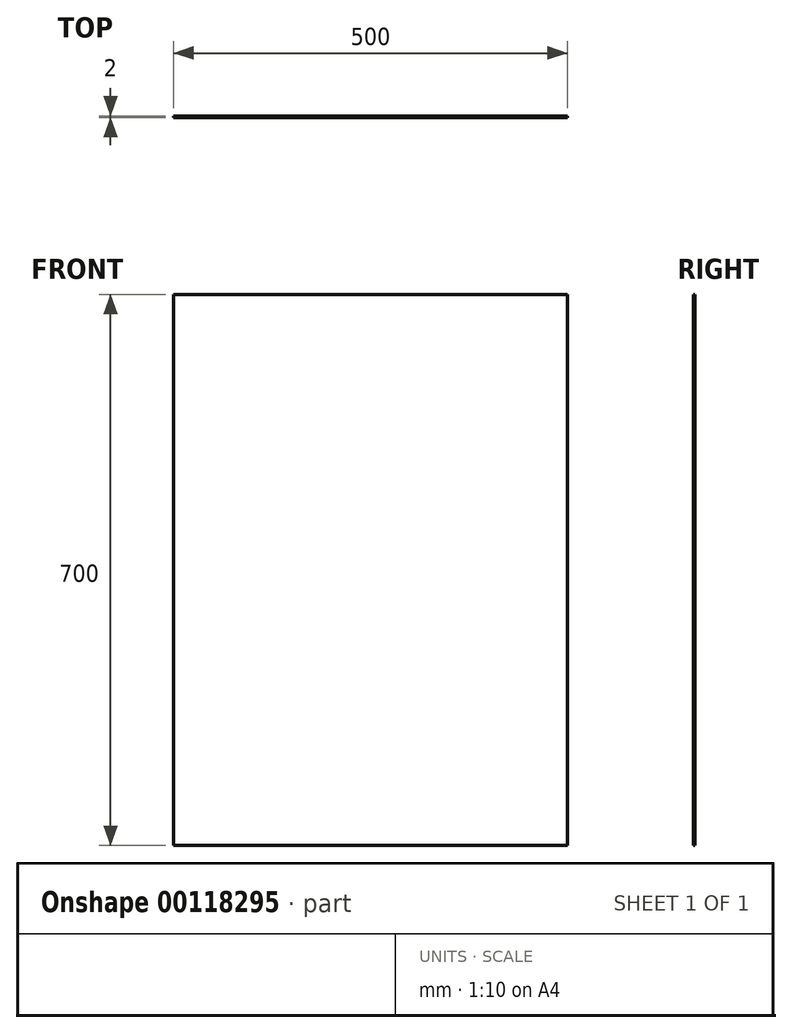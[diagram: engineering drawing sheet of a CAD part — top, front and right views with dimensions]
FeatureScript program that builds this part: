
annotation { "Feature Type Name" : "Feature", "Feature Type Description" : "" }
export const myFeature = defineFeature(function(context is Context, id is Id, definition is map)
    precondition{}
    {
        {
            var Q0;
            Q0=qCreatedBy(makeId("Front.planeOp"),FACE);
            var sketch = newSketch(context, id + "F0", { "sketchPlane" : qUnion([Q0])});
            skLineSegment(sketch, "E0.bottom", {"start": v(250, 350) * mm, "end": v(-250, 350) * mm});
            skLineSegment(sketch, "E0.top", {"start": v(250, -350) * mm, "end": v(-250, -350) * mm});
            skLineSegment(sketch, "E0.left", {"start": v(250, 350) * mm, "end": v(250, -350) * mm});
            skLineSegment(sketch, "E0.right", {"start": v(-250, 350) * mm, "end": v(-250, -350) * mm});
            skPoint(sketch, "E0.middle", {"position": v(0, 0) * mm});
            skSolve(sketch);
        }
        {
            var Q0;
            Q0 = qSketchRegion(id + "F0", true);
            var Q1;
            Q1=makeQuery(id+"F0.imprint","IMPRINT",FACE,{"disambiguationData":[TD([[makeQuery(id+"F0.imprint","IMPRINT",EDGE,{"derivedFrom":sQuery(id+"F0.wireOp",EDGE,"E0.bottom")}),1.0]])]});
            extrude(context, id + "F1", {"entities" : qUnion([Q0, Q1]), "depth" : 2 * mm});
        }
    });
